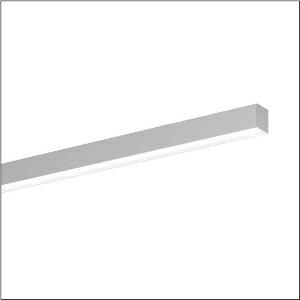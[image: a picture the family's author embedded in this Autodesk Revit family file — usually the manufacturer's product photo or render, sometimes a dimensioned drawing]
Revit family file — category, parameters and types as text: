
# Revit family: silica_21_51mx23dc3asb
name_source: partatom
category: Lighting Fixtures
units: mm (PartAtom-declared; Revit-internal decimal feet)

## family parameters
Cut with Voids When Loaded = No
Host = Face
Light Source = No
Part Type = Normal
Room Calculation Point = No
Round Connector Dimension = Use Diameter
Shared = No

## types (1)
- --- (1 x LED, 8200 lm, 62.2 W, 3000K)
    Apparent Load = 62 VA
    CIE Flux Codes = 78 96 99 100 100
    Color Rendering = 80
    Color Temperature = 3000K
    Default Elevation = 1800 mm
    Description = Silica 21, office luminaire, primary optical cover: prismatic diffuser, of PMMA, CAT 2 (L<= 3000cd/m²), light emission: direct distribution, primary light characteristic: symmetric, installation type: surface-mounted, LED, rated luminous flux: 8.200lm, luminous efficacy: 132lm/W, light colour: 830, colour temperature: 3000K, control gear: DALI 2, with terminal, 3+2-pole, max. 2.5mm², mains connection: 220..240V, AC, 50/60Hz, rated input power: 62.2W, luminaire housing, of aluminium, metallic grey (RAL 9006), length: 3.004mm, width: 53mm, height: 53mm, protection rating (complete): IP20, insulation class (complete): insulation class I (protective earthing), certification: CE, permissible operating ambient temperature: 0..+35°C, standard: EN 50419, packaging unit: 1 piece
    Height = 53 mm
    Lamp = 1 x LED
    Lamp Light Flux = 8200 lm
    Lamp Power = 62.2 W
    Lamp count = 1
    Length = 3004 mm
    Luminous efficacy = 132 lm/W
    Manufacturer = Siteco
    ModVariant = No
    Model = 51MX23DC3ASB
    Mounting Place = Ceiling
    Mounting Type = Surface mounted
    Number of Poles = 1
    OnlyDefault = Yes
    Power Factor = 1
    Product Name = Silica 21
    Product group = office luminaire | ceiling mounted
    ProductGroupID = 301
    Protection Class = Protection class I
    Protection Degree = IP 20
    RLX_Detail_Level = 1
    RLX_Emergency_Light_Flux = 0 lm
    RLX_Emergency_Type = 0
    RLX_Emergency_Type_DB = No
    RlxData = <blob elided: 21205 chars, md5=1b5c6ad3>
    Socket = socket
    Standby Power = 0 W
    System Light Flux = 8200 lm
    System Power = 62 W
    Type Comments = factory setting: luminous flux: 100 % | dim-lin: 254 | 345 mA
    Type Image = l_1335933.jpg
    URL = http://relux.com
    VarID = @adj_120851
    Voltage = 0 V
    Weight = 0.00 kg
    Width = 53 mm

## geometry (parser evidence)
native form markers: Blend x4, Sweep x13
no freeform markers — native parametric forms only
